# Revit family: Trapezblechhänger, VA
name_source: partatom
category: HLS-Bauteile
revit_build: Autodesk Revit 2017 (Build: 20190507_1515(x64)
units: mm (PartAtom-declared; Revit-internal decimal feet)

## family parameters
Arbeitsebenenbasiert = Ja
Beim Laden mit Abzugskörper schneiden = Nein
Bemaßung runder Anschluss = Durchmesser verwenden
Gemeinsam genutzt = Ja
Immer vertikal = Nein
Raumberechnungspunkt = Nein
Teiletyp = Normal

## types (4) — shared parameters
Ausführung = eingeschweißte Mutter
Befestigungsloch = 9 mm
Breite Aufnahme (innen) = 30 mm
Breite Material = 25 mm
Fabrikat = MEFA
Firma = MEFA Befestigungs- und Montagesysteme GmbH
Höhe = 97 mm
Material = Edelstahl
Mengeneinheit = St
Vorgabe-Ansicht = 1219 mm
max. zul. Last = 2.00 kN
vpe = 1 St
zero-valued in all types: Stärke Material

## per-type parameters (varying)
| type | Anschlussgewinde | Artikelnummer | EAN | Gewicht | Gewicht pro Bauteil | Kurztext1 | Kurztext2 | Sechskantmutter |
| Trapezblechhänger M 8, V2A | M8 | 0783961 | 4250928418876 | 0.13 kg | 0.13 kg | Trapezblechhänger MU-S V2A | eingeschweißte Mutter M8 | Sechskantmutter VA : Sechskantmutter M 8 V2A |
| Trapezblechhänger M 8, V4A | M8 | 0783971 | 4250928418890 | 0.13 kg | 0.13 kg | Trapezblechhänger MU-S V4A | eingeschweißte Mutter M8 | Sechskantmutter VA : Sechskantmutter M 8 V4A |
| Trapezblechhänger M10, V2A | M10 | 0783962 | 4250928418883 | 0.14 kg | 0.14 kg | Trapezblechhänger MU-S V2A | eingeschweißte Mutter M10 | Sechskantmutter VA : Sechskantmutter M10 V2A |
| Trapezblechhänger M10, V4A | M10 | 0783972 | 4250928418906 | 0.14 kg | 0.14 kg | Trapezblechhänger MU-S V4A | eingeschweißte Mutter M10 | Sechskantmutter VA : Sechskantmutter M10 V4A |

## geometry (parser evidence)
native form markers: Sweep x3
no freeform markers — native parametric forms only
